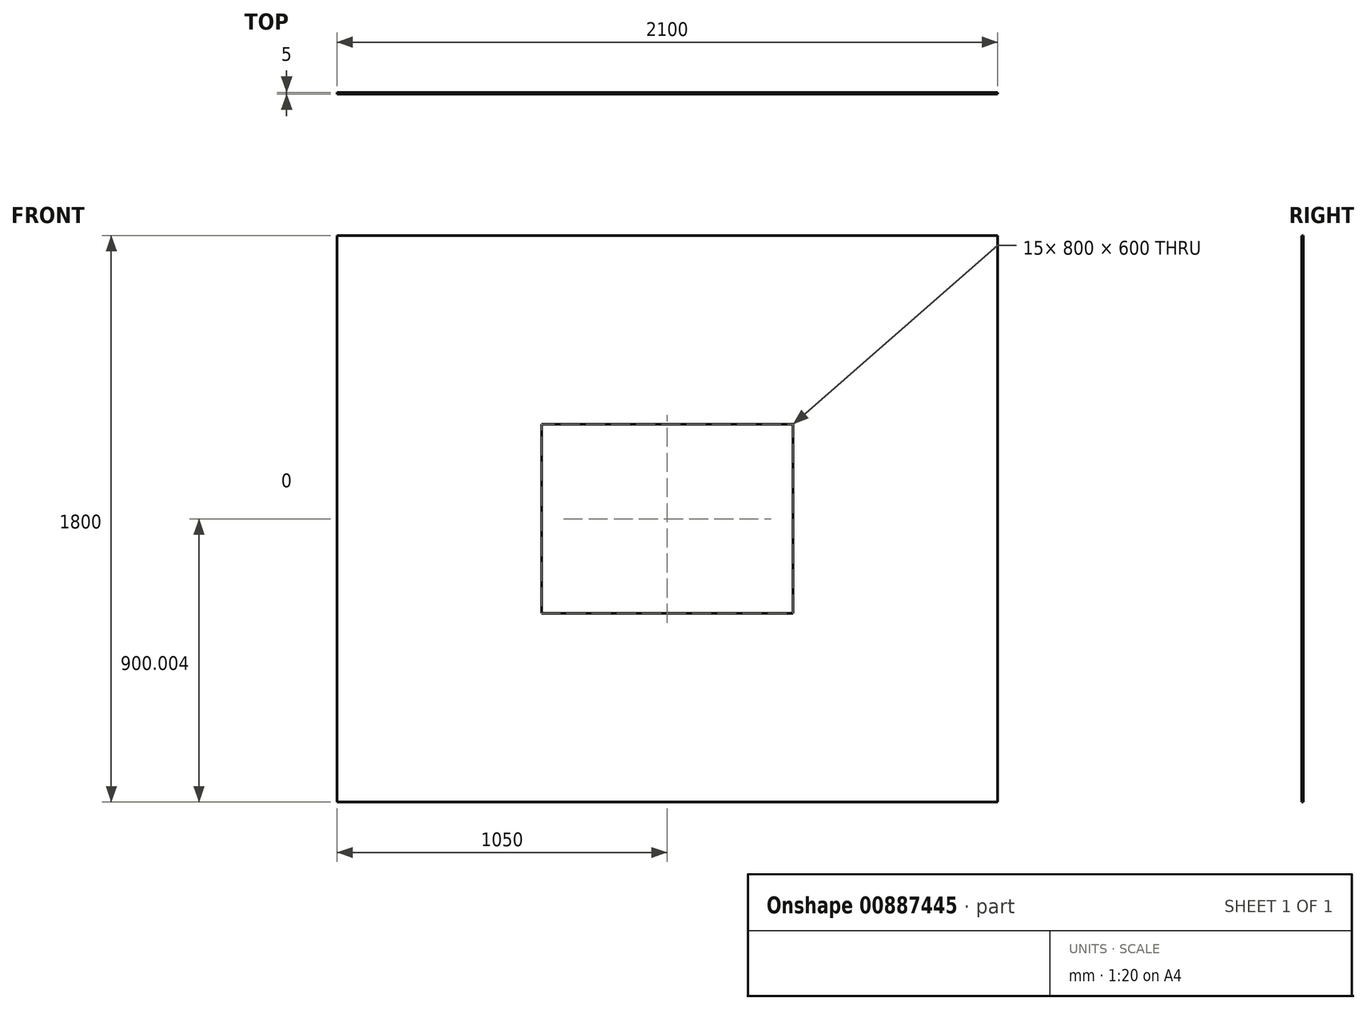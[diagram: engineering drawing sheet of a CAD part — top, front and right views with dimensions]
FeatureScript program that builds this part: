
annotation { "Feature Type Name" : "Feature", "Feature Type Description" : "" }
export const myFeature = defineFeature(function(context is Context, id is Id, definition is map)
    precondition{}
    {
        {
            var Q0;
            Q0=qCreatedBy(makeId("Front.planeOp"),FACE);
            var sketch = newSketch(context, id + "F0", { "sketchPlane" : qUnion([Q0])});
            skLineSegment(sketch, "E0.bottom", {"start": v(-650, -434.83) * mm, "end": v(1450, -434.83) * mm});
            skLineSegment(sketch, "E0.top", {"start": v(-650, 1365.17) * mm, "end": v(1450, 1365.17) * mm});
            skLineSegment(sketch, "E0.left", {"start": v(-650, -434.83) * mm, "end": v(-650, 1365.17) * mm});
            skLineSegment(sketch, "E0.right", {"start": v(1450, -434.83) * mm, "end": v(1450, 1365.17) * mm});
            skLineSegment(sketch, "E1.bottom", {"start": v(0, 765.17) * mm, "end": v(800, 765.17) * mm});
            skLineSegment(sketch, "E1.top", {"start": v(0, 165.17) * mm, "end": v(800, 165.17) * mm});
            skLineSegment(sketch, "E1.left", {"start": v(0, 765.17) * mm, "end": v(0, 165.17) * mm});
            skLineSegment(sketch, "E1.right", {"start": v(800, 765.17) * mm, "end": v(800, 165.17) * mm});
            skSolve(sketch);
        }
        {
            var Q0;
            Q0=makeQuery(id+"F0.imprint","IMPRINT",FACE,{"disambiguationData":[TD([[makeQuery(id+"F0.imprint","IMPRINT",EDGE,{"derivedFrom":sQuery(id+"F0.wireOp",EDGE,"E0.bottom")}),1.0]])]});
            extrude(context, id + "F1", {"entities" : qUnion([Q0]), "endBound" : BoundingType.SYMMETRIC, "depth" : 5 * mm, "offsetDistance" : 25 * mm});
        }
    });
